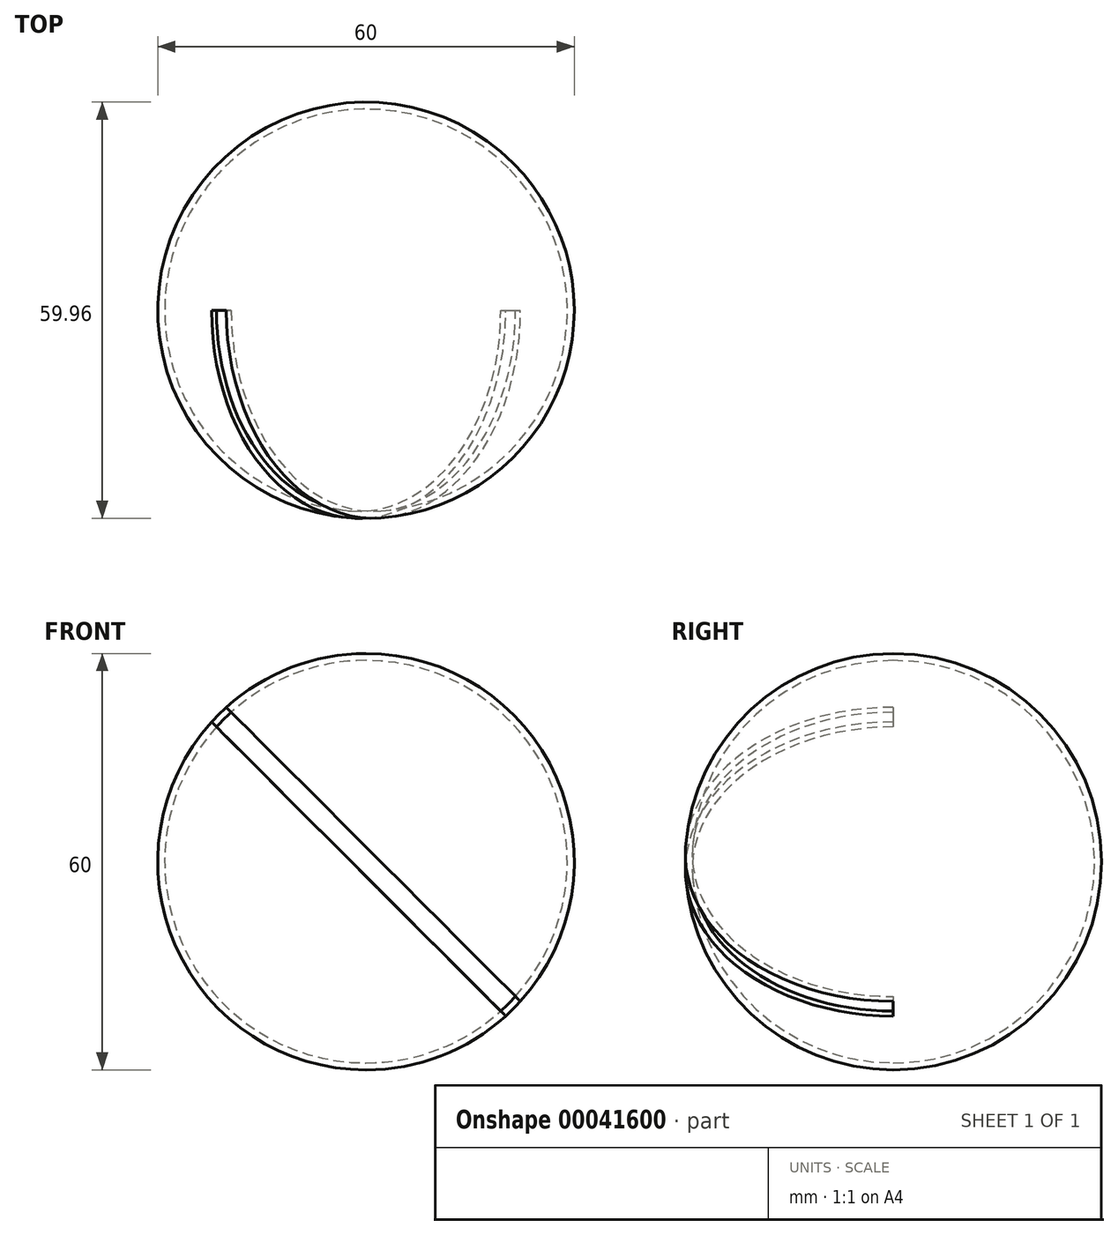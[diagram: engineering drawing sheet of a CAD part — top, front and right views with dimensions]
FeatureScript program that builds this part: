
annotation { "Feature Type Name" : "Feature", "Feature Type Description" : "" }
export const myFeature = defineFeature(function(context is Context, id is Id, definition is map)
    precondition{}
    {
        {
            var Q0;
            Q0=qCreatedBy(makeId("Right.planeOp"),FACE);
            var sketch = newSketch(context, id + "F0", { "sketchPlane" : qUnion([Q0])});
            skArc(sketch, "E0", {"start": v(0, 30) * mm, "mid": v(-30, 0) * mm, "end": v(0, -30) * mm});
            skArc(sketch, "E1", {"start": v(0, 29) * mm, "mid": v(-29, 0) * mm, "end": v(0, -29) * mm});
            skLineSegment(sketch, "E2", {"start": v(0, 32.67) * mm, "end": v(0, -36.38) * mm, "construction": true});
            skLineSegment(sketch, "E3", {"start": v(0, 30) * mm, "end": v(0, 29) * mm});
            skLineSegment(sketch, "E4", {"start": v(0, -29) * mm, "end": v(0, -30) * mm});
            skSolve(sketch);
        }
        {
            var Q0;
            Q0=makeQuery(id+"F0.imprint","IMPRINT",FACE,{"disambiguationData":[TD([[makeQuery(id+"F0.imprint","IMPRINT",EDGE,{"derivedFrom":sQuery(id+"F0.wireOp",EDGE,"E0")}),1.0]])]});
            var Q1;
            Q1=sQuery(id+"F0.wireOp",EDGE,"E2");
            revolve(context, id + "F1", {"entities" : qUnion([Q0]), "axis" : qUnion([Q1]), "revolveType" : RevolveType.FULL});
        }
        {
            var Q0;
            Q0=qCreatedBy(makeId("Front.planeOp"),FACE);
            var sketch = newSketch(context, id + "F2", { "sketchPlane" : qUnion([Q0])});
            skLineSegment(sketch, "E5.bottom", {"start": v(-25.8, 23.69) * mm, "end": v(-23.69, 25.8) * mm});
            skLineSegment(sketch, "E5.top", {"start": v(23.69, -25.8) * mm, "end": v(25.8, -23.69) * mm});
            skLineSegment(sketch, "E5.left", {"start": v(-25.8, 23.69) * mm, "end": v(23.69, -25.8) * mm});
            skLineSegment(sketch, "E5.right", {"start": v(-23.69, 25.8) * mm, "end": v(25.8, -23.69) * mm});
            skLineSegment(sketch, "E6", {"start": v(-24.75, 24.75) * mm, "end": v(24.75, -24.75) * mm, "construction": true});
            skSolve(sketch);
        }
        {
            var Q0;
            Q0=makeQuery(id+"F2.imprint","IMPRINT",FACE,{"disambiguationData":[TD([[makeQuery(id+"F2.imprint","IMPRINT",EDGE,{"derivedFrom":sQuery(id+"F2.wireOp",EDGE,"E5.bottom")}),-1.0]])]});
            extrude(context, id + "F3", {"entities" : qUnion([Q0]), "depth" : 30 * mm});
        }
        {
            var Q0;
            Q0=makeQuery(id+"F3.opExtrude","SWEPT_BODY",BODY,{"disambiguationData":[OSD([sQuery(id+"F2.wireOp",EDGE,"E5.bottom"),sQuery(id+"F2.wireOp",EDGE,"E5.top"),sQuery(id+"F2.wireOp",EDGE,"E5.left"),sQuery(id+"F2.wireOp",EDGE,"E5.right")])]});
            var Q1;
            Q1=makeQuery(id+"F1.opRevolve","SWEPT_BODY",BODY,{"disambiguationData":[OSD([sQuery(id+"F0.wireOp",EDGE,"E0"),sQuery(id+"F0.wireOp",EDGE,"E1"),sQuery(id+"F0.wireOp",EDGE,"E3"),sQuery(id+"F0.wireOp",EDGE,"E4")])]});
            booleanBodies(context, id + "F4", {"operationType" : BooleanOperationType.SUBTRACTION, "tools" : qUnion([Q0]), "targets" : qUnion([Q1])});
        }
    });
